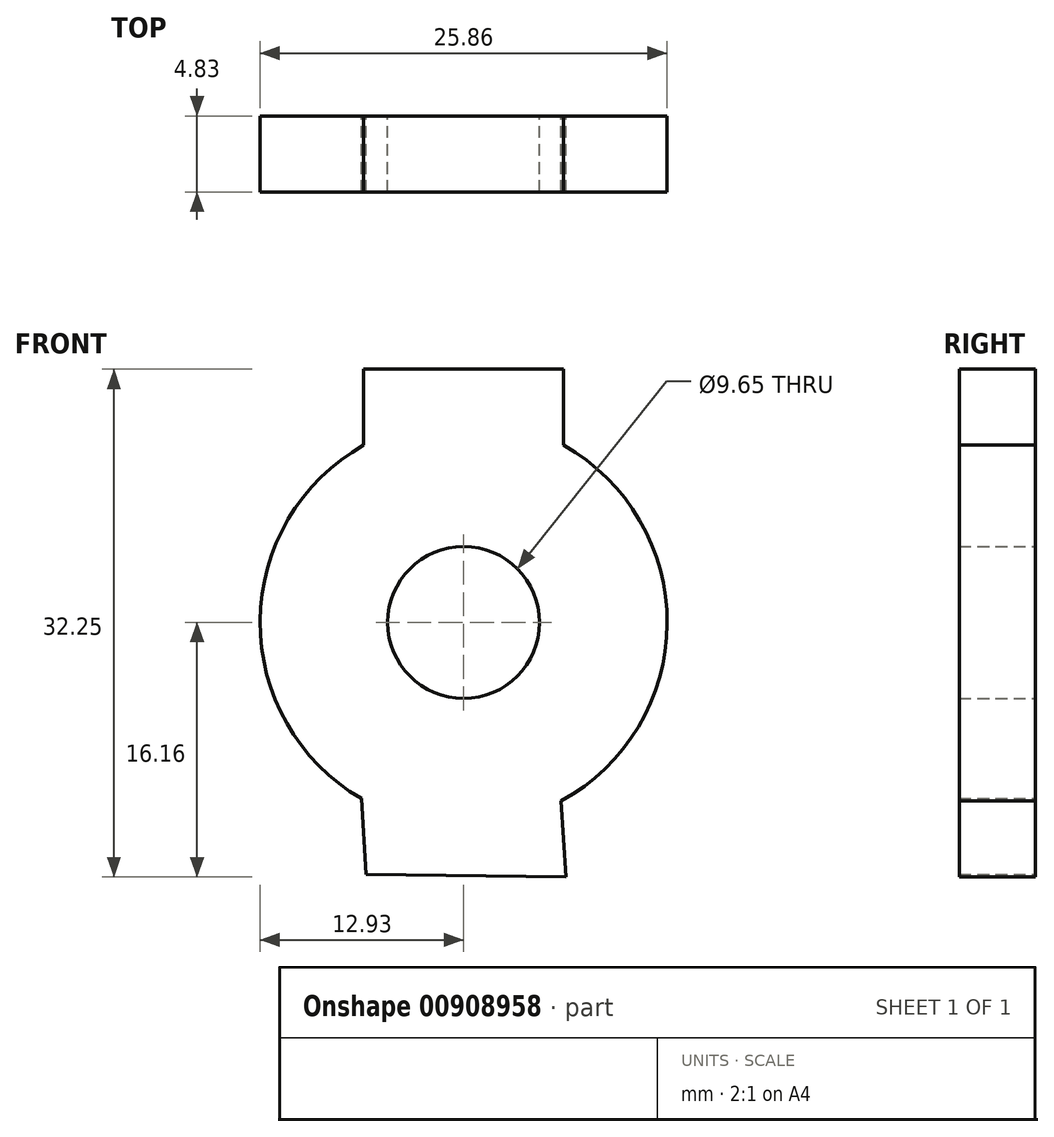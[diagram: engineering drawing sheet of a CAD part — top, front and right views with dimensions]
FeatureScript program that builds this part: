
annotation { "Feature Type Name" : "Feature", "Feature Type Description" : "" }
export const myFeature = defineFeature(function(context is Context, id is Id, definition is map)
    precondition{}
    {
        {
            var Q0;
            Q0=qCreatedBy(makeId("Front.planeOp"),FACE);
            var sketch = newSketch(context, id + "F0", { "sketchPlane" : qUnion([Q0])});
            skLineSegment(sketch, "E0.bottom", {"start": v(6.5, -16.16) * mm, "end": v(-6.2, -16) * mm});
            skLineSegment(sketch, "E0.left", {"start": v(6.5, -16.16) * mm, "end": v(6.2, -11.34) * mm});
            skLineSegment(sketch, "E0.right", {"start": v(-6.2, -16) * mm, "end": v(-6.5, -11.18) * mm});
            skPoint(sketch, "E0.middle", {"position": v(0, -13.67) * mm});
            skArc(sketch, "E1", {"start": v(6.2, -11.34) * mm, "mid": v(12.93, -0.09) * mm, "end": v(6.35, 11.26) * mm});
            skPoint(sketch, "E2.center", {"position": v(0, -0.04) * mm});
            skLineSegment(sketch, "E3.top", {"start": v(6.35, 16.09) * mm, "end": v(-6.35, 16.09) * mm});
            skLineSegment(sketch, "E3.left", {"start": v(6.35, 11.26) * mm, "end": v(6.35, 16.09) * mm});
            skLineSegment(sketch, "E3.right", {"start": v(-6.35, 11.26) * mm, "end": v(-6.35, 16.09) * mm});
            skPoint(sketch, "E3.middle", {"position": v(0, 13.67) * mm});
            skCircle(sketch, "E4", {"center": v(0, 0) * mm, "radius": 4.83 * mm});
            skArc(sketch, "E5.trimOffspring", {"start": v(-6.35, 11.26) * mm, "mid": v(-12.93, 0.09) * mm, "end": v(-6.5, -11.18) * mm});
            skSolve(sketch);
        }
        {
            var Q0;
            Q0=makeQuery(id+"F0.imprint","IMPRINT",FACE,{"disambiguationData":[TD([[makeQuery(id+"F0.imprint","IMPRINT",EDGE,{"derivedFrom":sQuery(id+"F0.wireOp",EDGE,"E0.bottom")}),-1.0]])]});
            extrude(context, id + "F1", {"entities" : qUnion([Q0]), "depth" : 4.83 * mm, "offsetDistance" : 25.4 * mm});
        }
    });
